# Revit family: Pump_Commercial-Effluent-Zoeller-4161_Series
name_source: partatom
category: Mechanical Equipment
units: mm (PartAtom-declared; Revit-internal decimal feet)

## family parameters
Always vertical = No
Cut with Voids When Loaded = No
OmniClass Number = 23.60.30.21
OmniClass Title = Pumps
Part Type = Normal
Room Calculation Point = No
Round Connector Dimension = Use Radius
Shared = Yes
Work Plane-Based = Yes

## types (18) — shared parameters
Assembly Code = D2010900
Cooling = Oil Filled
Cord Length = 240"
Cord Type = UL listed, 3-wire neoprene cord and plug (1 Ph) or 4-wire cord with no plug (3 Ph)
Default Elevation = 0"
Description = Double Seal High Head Commercial Effluent Pumps
Discharge Diameter = 1-1/2" NPT (optional 2" or 3" flange)
Discharge Height = 6"
Discharge Radius = 3/4"
Height = 21 3/16"
Hertz = 60
Impeller = Cast Iron
Impeller Type = Non-clogging vortex
Installation Type = Floor Mounted
Insulation = Class B
Lead Wires Insulation = Class B
Length = 12 3/4"
Manufacturer = Zoeller
Masterformat Number = 33 36 16
Masterformat Title = Utility Septic Tank Effluent Pumps
Material = Cast Iron-Zoeller-Powder Coated Epoxy
Max. Operating Temp. = 130.00 °F
Min. Recommended Fluid Level = 10"
Minimum Head = 60"
Motor Design Letter = NEMA B
Motor Thermal Shutoff (Single Phase Only) = Thermal Overload Sensors With Automatic Reset.
Motor Type = Submersible
Omniclass Table 23 Code = 23.60.30.21
Omniclass Table 23 Title = Pumps
Operation = Non-Automatic
Price = Prices may vary. Please consult Manufacturer Representative for most up-to-date price list.
Product Page URL = http://www.zoellerpumps.com
RPM = 3450
Shaft Seal = Carbon and Ceramic
Shipping Weight = 87 lbs
Solid Handling = 3/4" Spherical Solids
Square Ring & Gasket = Neoprene
URL = http://www.zoellerpumps.com
Warranty Information = 36 Months (Limited)
Waste Connection = Yes
Width = 8"

## per-type parameters (varying)
| type | Amps | Apparent Load | Flow @ 5' | Maximum Head | Model | Motor | Phase | Type | Voltage |
| 4161-115V 1Ph | 16 A | 1783 VA | 100 GPM | 672" | 4161 | 1/2 HP | 1 | Permanent Split Capacitor | 115 V |
| 4163-115V 1Ph | 15 A | 1725 VA | 61 GPM | 792" | 4163 | 1/2 HP | 1 | Permanent Split Capacitor | 115 V |
| 4163-230V 1Ph | 8 A | 1725 VA | 61 GPM | 792" | 4163 | 1/2 HP | 1 | Permanent Split Capacitor | 230 V |
| 4163-200V 1Ph | 9 A | 1700 VA | 61 GPM | 792" | 4163 | 1/2 HP | 1 | Permanent Split Capacitor | 200 V |
| 4163-208V 1Ph | 9 A | 1768 VA | 61 GPM | 792" | 4163 | 1/2 HP | 1 | Permanent Split Capacitor | 208 V |
| 4163-200V 3Ph | 6 A | 1200 VA | 61 GPM | 792" | 4163 | 1/2 HP | 3 | 3 Phase | 200 V |
| 4163-208V 3Ph | 6 A | 1248 VA | 61 GPM | 792" | 4163 | 1/2 HP | 3 | 3 Phase | 208 V |
| 4163-230V 3Ph | 5 A | 1104 VA | 61 GPM | 792" | 4163 | 1/2 HP | 3 | 3 Phase | 230 V |
| 4163-460V 3Ph | 3 A | 1334 VA | 61 GPM | 792" | 4163 | 1/2 HP | 3 | 3 Phase | 460 V |
| 4163-575V 3Ph | 2 A | 1380 VA | 61 GPM | 792" | 4163 | 1/2 HP | 3 | 3 Phase | 575 V |
| 4165-230V 1Ph | 10 A | 2346 VA | 61 GPM | 1038" | 4165 | 1 HP | 1 | Permanent Split Capacitor | 230 V |
| 4165-200V 1Ph | 13 A | 2520 VA | 61 GPM | 1038" | 4165 | 1 HP | 1 | Permanent Split Capacitor | 200 V |
| 4165-208V 1Ph | 13 A | 2621 VA | 61 GPM | 1038" | 4165 | 1 HP | 1 | Permanent Split Capacitor | 208 V |
| 4165-200V 3Ph | 8 A | 1500 VA | 61 GPM | 1038" | 4165 | 1 HP | 3 | 3 Phase | 200 V |
| 4165-208V 3Ph | 8 A | 1560 VA | 61 GPM | 1038" | 4165 | 1 HP | 3 | 3 Phase | 208 V |
| 4165-230V 3Ph | 7 A | 1702 VA | 61 GPM | 1038" | 4165 | 1 HP | 3 | 3 Phase | 230 V |
| 4165-460V 3Ph | 4 A | 1702 VA | 61 GPM | 1038" | 4165 | 1 HP | 3 | 3 Phase | 460 V |
| 4165-575V 3Ph | 3 A | 1725 VA | 61 GPM | 1038" | 4165 | 1 HP | 3 | 3 Phase | 575 V |

## geometry (parser evidence)
native form markers: Blend x4, Sweep x2
no freeform markers — native parametric forms only
